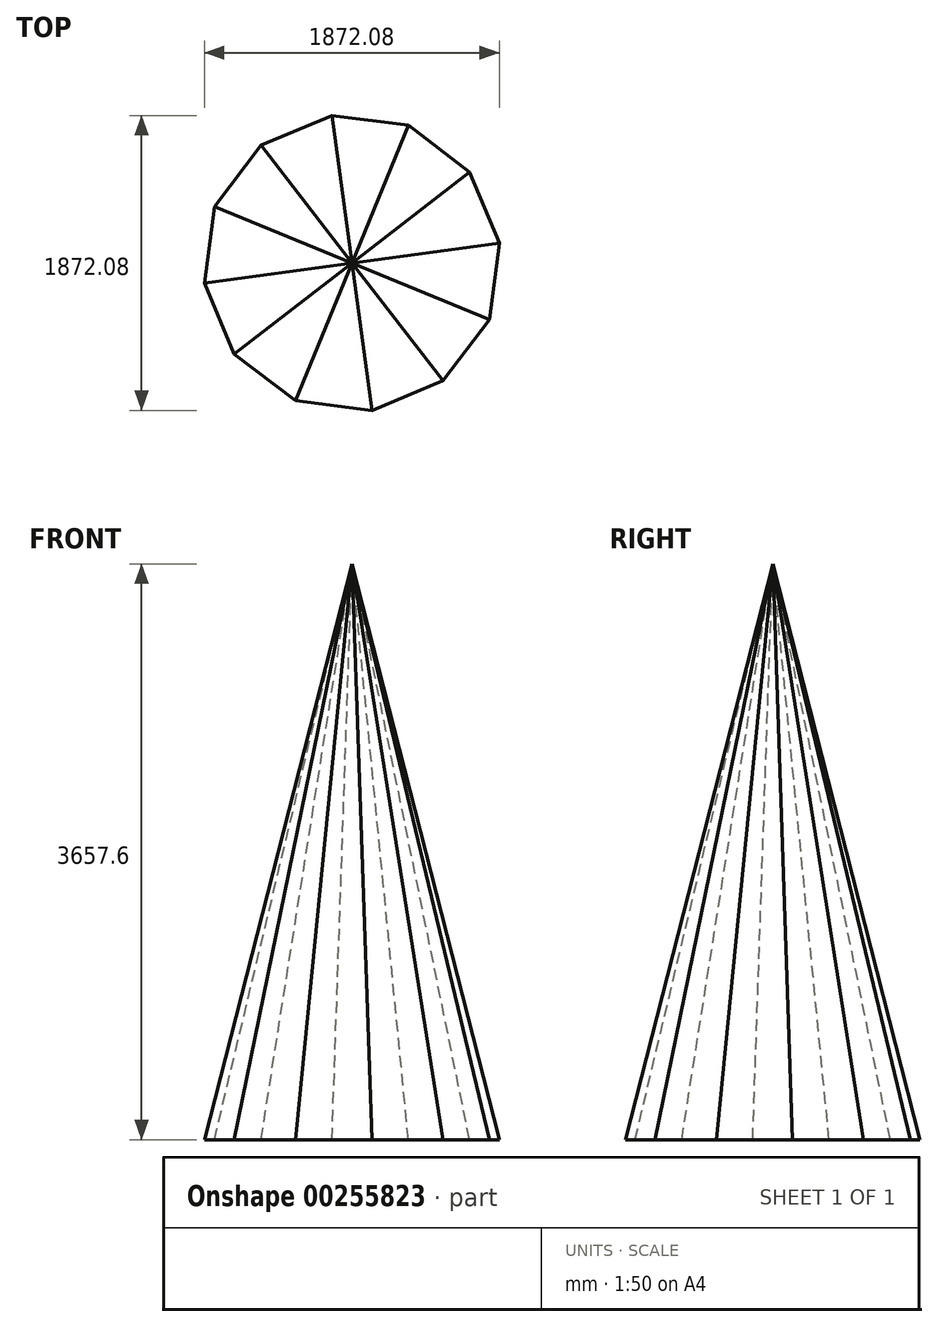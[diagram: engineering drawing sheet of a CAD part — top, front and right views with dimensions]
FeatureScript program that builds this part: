
annotation { "Feature Type Name" : "Feature", "Feature Type Description" : "" }
export const myFeature = defineFeature(function(context is Context, id is Id, definition is map)
    precondition{}
    {
        {
            var Q0;
            Q0=qCreatedBy(makeId("Top.planeOp"),FACE);
            var sketch = newSketch(context, id + "F0", { "sketchPlane" : qUnion([Q0])});
            skCircle(sketch, "E0.cCircle", {"center": v(0, 0) * mm, "radius": 944.58 * mm, "construction": true});
            skLineSegment(sketch, "E0.0", {"start": v(874, -358.28) * mm, "end": v(577.76, -747.28) * mm});
            skLineSegment(sketch, "E0.1", {"start": v(577.76, -747.28) * mm, "end": v(126.71, -936.04) * mm});
            skLineSegment(sketch, "E0.2", {"start": v(126.71, -936.04) * mm, "end": v(-358.28, -874) * mm});
            skLineSegment(sketch, "E0.3", {"start": v(-358.28, -874) * mm, "end": v(-747.28, -577.76) * mm});
            skLineSegment(sketch, "E0.4", {"start": v(-747.28, -577.76) * mm, "end": v(-936.04, -126.71) * mm});
            skLineSegment(sketch, "E0.5", {"start": v(-936.04, -126.71) * mm, "end": v(-874, 358.28) * mm});
            skLineSegment(sketch, "E0.6", {"start": v(-874, 358.28) * mm, "end": v(-577.76, 747.28) * mm});
            skLineSegment(sketch, "E0.7", {"start": v(-577.76, 747.28) * mm, "end": v(-126.71, 936.04) * mm});
            skLineSegment(sketch, "E0.8", {"start": v(-126.71, 936.04) * mm, "end": v(358.28, 874) * mm});
            skLineSegment(sketch, "E0.9", {"start": v(358.28, 874) * mm, "end": v(747.28, 577.76) * mm});
            skLineSegment(sketch, "E0.10", {"start": v(747.28, 577.76) * mm, "end": v(936.04, 126.71) * mm});
            skLineSegment(sketch, "E0.11", {"start": v(936.04, 126.71) * mm, "end": v(874, -358.28) * mm});
            skSolve(sketch);
        }
        {
            var Q0;
            Q0=qCreatedBy(makeId("Front.planeOp"),FACE);
            var sketch = newSketch(context, id + "F1", { "sketchPlane" : qUnion([Q0])});
            skPoint(sketch, "E1", {"position": v(0, 3657.6) * mm});
            skSolve(sketch);
        }
        {
            var Q0;
            Q0=makeQuery(id+"F0.imprint","IMPRINT",FACE,{"disambiguationData":[TD([[makeQuery(id+"F0.imprint","IMPRINT",EDGE,{"derivedFrom":sQuery(id+"F0.wireOp",EDGE,"E0.0")}),-1.0]])]});
            var Q1;
            Q1=sQuery(id+"F1.wireOp",VERTEX,"E1");
            loft(context, id + "F2", {"sheetProfilesArray" : [{ "sheetProfileEntities" : qUnion([Q0]) }, { "sheetProfileEntities" : qUnion([Q1]) }]});
        }
    });
